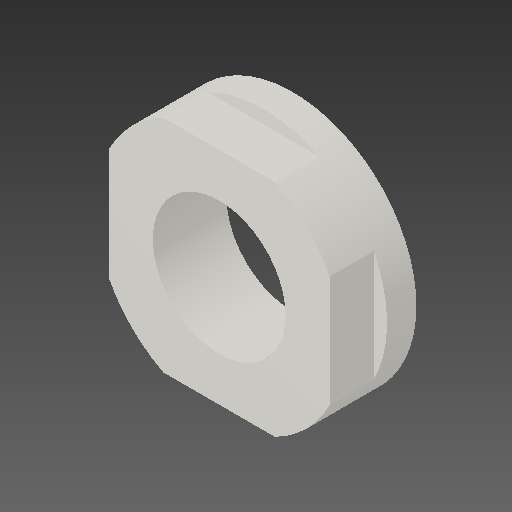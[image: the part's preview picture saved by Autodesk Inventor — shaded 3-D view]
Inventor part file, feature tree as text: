
AUTODESK INVENTOR PART (.ipt)
format: ipt  version: 2018 (Build 220112000, 112)  size: 114,176 bytes
history: native  units: mm
features: extrude x2, sketch x2
ambient origin geometry x8: Origin, YZ Plane, XZ Plane, XY Plane, X Axis, Y Axis, Z Axis, Center Point
bodies: Solid1 (feature_tree)
feature tree (4):
  extrude  "Extrusion1"  Depth=16.8mm
  extrude  "Extrusion2"  Depth=15.0mm
  sketch  "Sketch1"  dims[d0=9.02mm d1=16.8mm]
  sketch  "Sketch2"  dims[d2=5.0mm d3=0.0mm d4=15.0mm d5=3.0mm d6=0.0mm]
